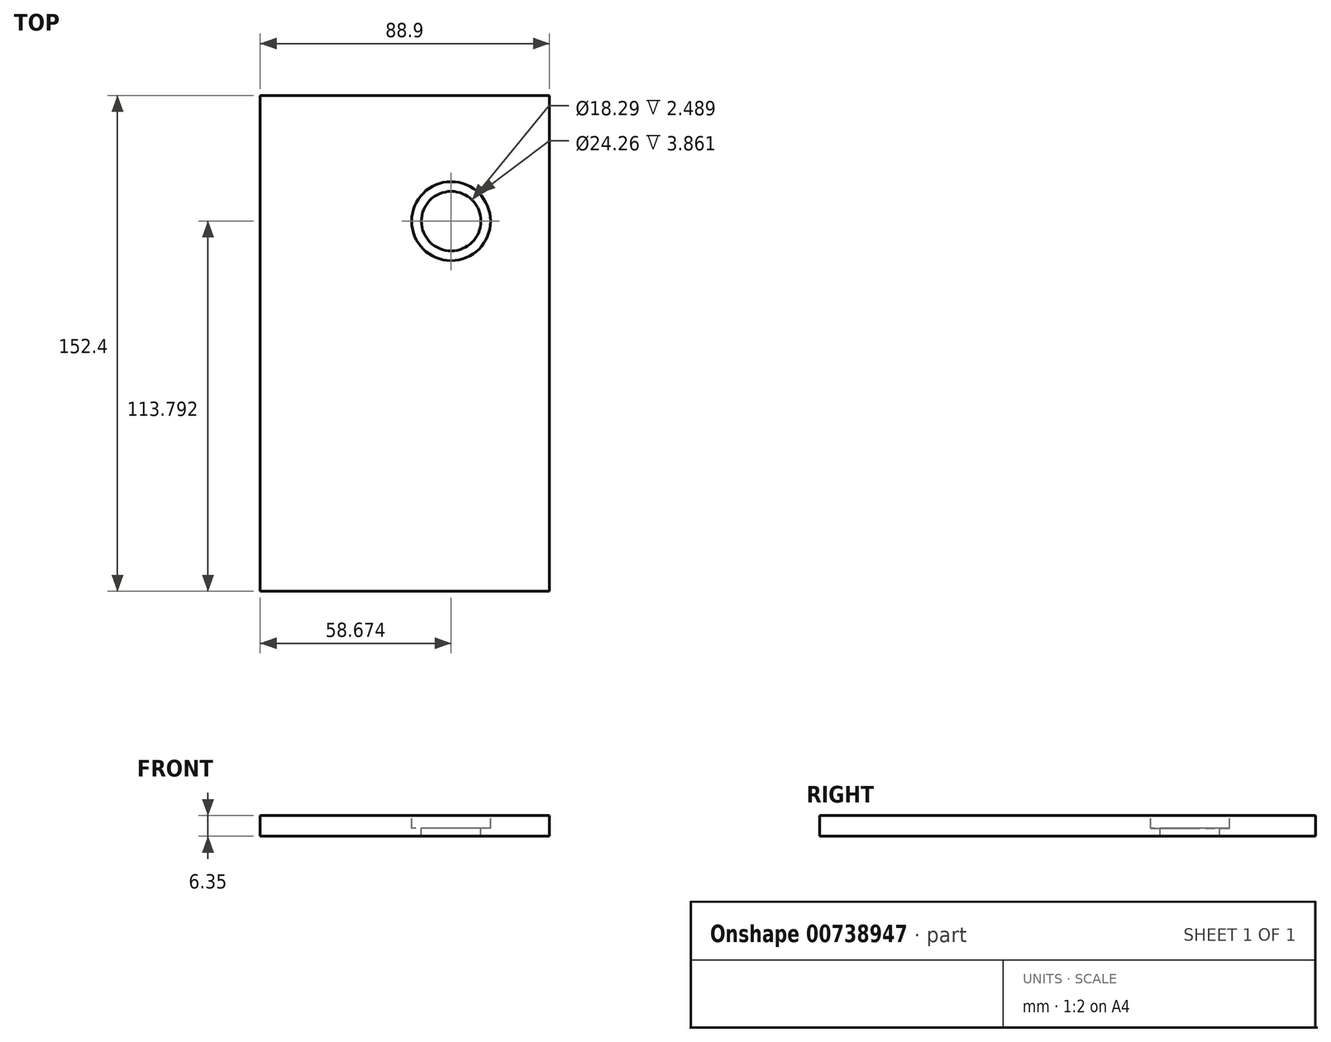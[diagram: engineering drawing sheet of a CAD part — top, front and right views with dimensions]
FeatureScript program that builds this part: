
annotation { "Feature Type Name" : "Feature", "Feature Type Description" : "" }
export const myFeature = defineFeature(function(context is Context, id is Id, definition is map)
    precondition{}
    {
        {
            var Q0;
            Q0=qCreatedBy(makeId("Top.planeOp"),FACE);
            var sketch = newSketch(context, id + "F0", { "sketchPlane" : qUnion([Q0])});
            skLineSegment(sketch, "E0.bottom", {"start": v(44.45, -76.2) * mm, "end": v(-44.45, -76.2) * mm});
            skLineSegment(sketch, "E0.top", {"start": v(44.45, 76.2) * mm, "end": v(-44.45, 76.2) * mm});
            skLineSegment(sketch, "E0.left", {"start": v(44.45, -76.2) * mm, "end": v(44.45, 76.2) * mm});
            skLineSegment(sketch, "E0.right", {"start": v(-44.45, -76.2) * mm, "end": v(-44.45, 76.2) * mm});
            skPoint(sketch, "E0.middle", {"position": v(0, 0) * mm});
            skSolve(sketch);
        }
        {
            var Q0;
            Q0 = qSketchRegion(id + "F0", true);
            extrude(context, id + "F1", {"entities" : qUnion([Q0]), "depth" : 6.35 * mm, "offsetDistance" : 25.4 * mm});
        }
        {
            var Q0;
            Q0=makeQuery(id+"F1.opExtrude","CAP_FACE",FACE,{"disambiguationData":[OSD([sQuery(id+"F0.wireOp",EDGE,"E0.bottom"),sQuery(id+"F0.wireOp",EDGE,"E0.top"),sQuery(id+"F0.wireOp",EDGE,"E0.left"),sQuery(id+"F0.wireOp",EDGE,"E0.right")])],"isStart":false});
            var sketch = newSketch(context, id + "F2", { "sketchPlane" : qUnion([Q0])});
            skPoint(sketch, "E1", {"position": v(14.22, 37.6) * mm});
            skLineSegment(sketch, "E2", {"start": v(14.22, 76.2) * mm, "end": v(14.22, 37.6) * mm});
            skLineSegment(sketch, "E3", {"start": v(44.45, 37.6) * mm, "end": v(14.22, 37.6) * mm});
            skSolve(sketch);
        }
        {
            var Q0;
            Q0=sQuery(id+"F2.wireOp",VERTEX,"E1");
            var Q1;
            Q1=makeQuery(id+"F1.opExtrude","SWEPT_BODY",BODY,{"disambiguationData":[OSD([sQuery(id+"F0.wireOp",EDGE,"E0.bottom"),sQuery(id+"F0.wireOp",EDGE,"E0.top"),sQuery(id+"F0.wireOp",EDGE,"E0.left"),sQuery(id+"F0.wireOp",EDGE,"E0.right")])]});
            hole(context, id + "F3", {"style" : HoleStyle.C_BORE, "endStyle" : HoleEndStyle.THROUGH, "holeDiameter" : 18.29 * mm, "cBoreDiameter" : 24.26 * mm, "cBoreDepth" : 3.86 * mm, "majorDiameter" : 6.35 * mm, "isTappedThrough" : true, "tappedDepth" : 12.7 * mm, "tapClearance" : 3, "locations" : qUnion([Q0]), "scope" : qUnion([Q1])});
        }
    });
